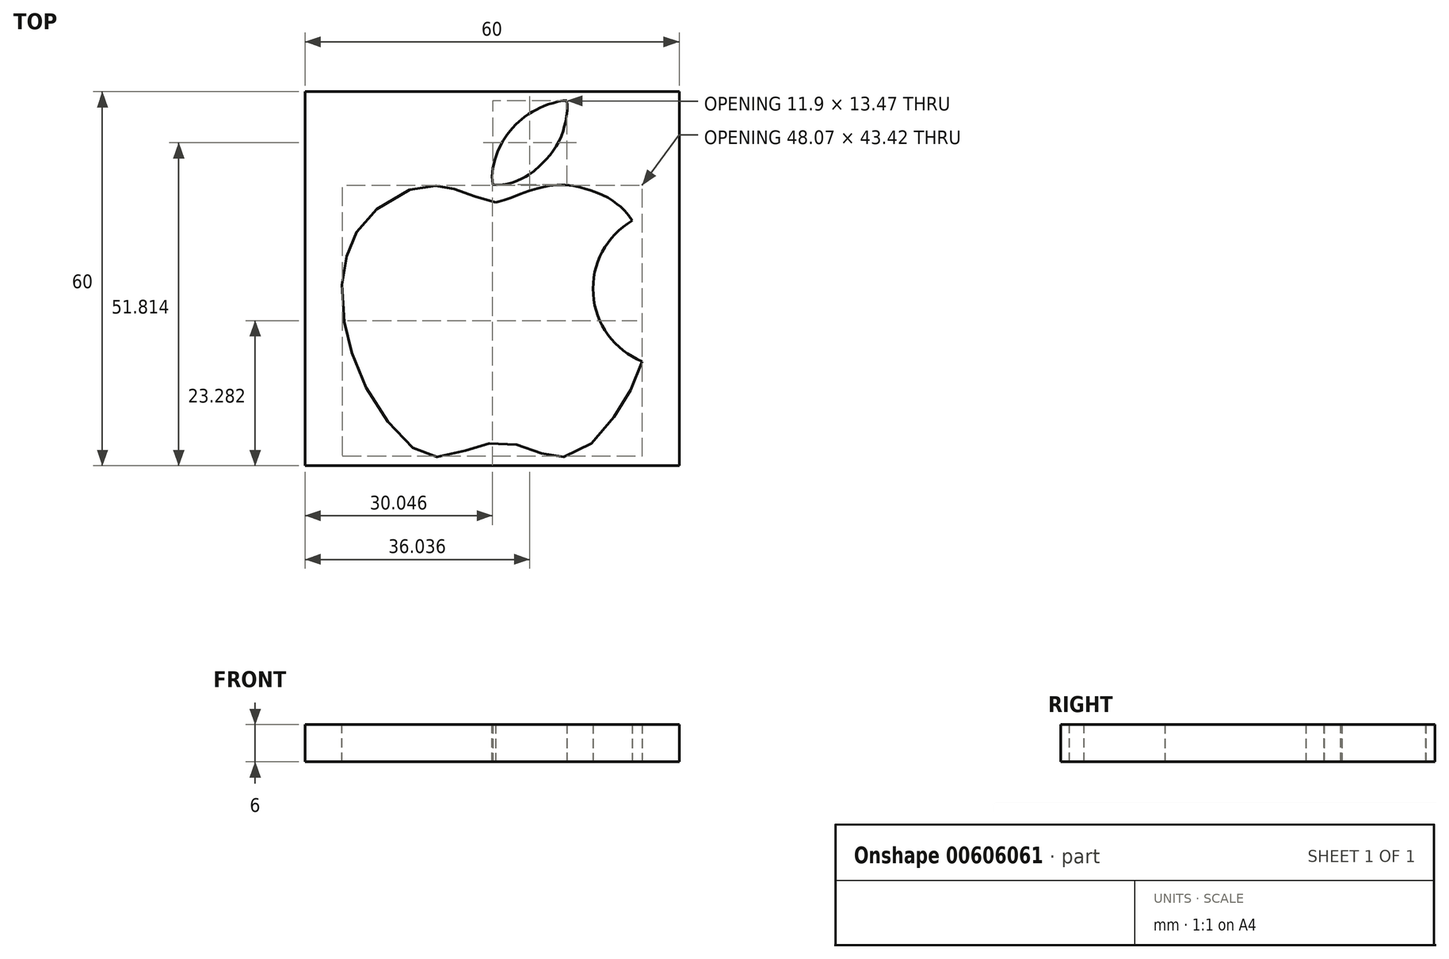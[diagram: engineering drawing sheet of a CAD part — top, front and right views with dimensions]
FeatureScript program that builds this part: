
annotation { "Feature Type Name" : "Feature", "Feature Type Description" : "" }
export const myFeature = defineFeature(function(context is Context, id is Id, definition is map)
    precondition{}
    {
        {
            var Q0;
            Q0=qCreatedBy(makeId("Top.planeOp"),FACE);
            var sketch = newSketch(context, id + "F0", { "sketchPlane" : qUnion([Q0])});
            skArc(sketch, "E0", {"start": v(52.5, 39.31) * mm, "mid": v(46.21, 27.53) * mm, "end": v(54.08, 16.73) * mm});
            skFitSpline(sketch, "E1", {"points": [v(52.5, 39.31) * mm, v(51.55, 40.58) * mm, v(50.61, 41.51) * mm, v(49.89, 42.08) * mm, v(49.02, 42.74) * mm, v(47.59, 43.48) * mm, v(45.89, 44.16) * mm, v(45.13, 44.36) * mm, v(43.9, 44.71) * mm, v(41.52, 45.05) * mm, v(39.07, 44.9) * mm, v(37.73, 44.63) * mm, v(34.98, 43.77) * mm, v(32.17, 42.67) * mm, v(30.95, 42.32) * mm, v(30.54, 42.22) * mm], "startDerivative": vector(-15.07, 19.7) * mm, "endDerivative": vector(-10.88, -2.45) * mm});
            skFitSpline(sketch, "E2", {"points": [v(30.54, 42.22) * mm, v(29.98, 42.25) * mm, v(28.38, 42.84) * mm, v(27.14, 43.26) * mm, v(26.49, 43.5) * mm, v(24.74, 44.13) * mm, v(23.26, 44.54) * mm, v(22.5, 44.63) * mm, v(21.97, 44.79) * mm, v(20.45, 44.9) * mm, v(18.9, 44.63) * mm, v(16.42, 44.16) * mm, v(12.72, 42.25) * mm, v(10.18, 39.76) * mm, v(8.57, 37.95) * mm, v(7.63, 36.17) * mm, v(6.95, 34.5) * mm, v(6.4, 32.55) * mm, v(6.08, 30.67) * mm, v(5.91, 26.78) * mm, v(6.28, 23.1) * mm, v(6.9, 20.17) * mm, v(7.67, 17.64) * mm, v(9.16, 13.85) * mm, v(11.03, 10.37) * mm, v(13.95, 6.25) * mm, v(16.4, 3.55) * mm, v(18.6, 2.05) * mm, v(20.17, 1.5) * mm, v(22.01, 1.45) * mm, v(24.46, 1.98) * mm, v(26.58, 2.78) * mm, v(28.13, 3.32) * mm, v(29.78, 3.63) * mm, v(31.48, 3.76) * mm, v(34.02, 3.36) * mm, v(36.23, 2.58) * mm, v(37.73, 2.06) * mm, v(38.79, 1.74) * mm, v(40.1, 1.5) * mm, v(42, 1.51) * mm, v(44.3, 2.4) * mm, v(46.98, 4.6) * mm, v(49.23, 7.33) * mm, v(50.52, 9.22) * mm, v(52.16, 11.97) * mm, v(52.81, 13.42) * mm, v(54.08, 16.73) * mm], "startDerivative": vector(-45.4, -1.17) * mm, "endDerivative": vector(82.14, 213.58) * mm});
            skFitSpline(sketch, "E3", {"points": [v(30.09, 45.08) * mm, v(30.75, 45.03) * mm, v(32.08, 45.15) * mm, v(32.98, 45.36) * mm, v(33.95, 45.68) * mm, v(34.8, 46.1) * mm, v(35.37, 46.38) * mm, v(35.9, 46.7) * mm, v(37.35, 47.82) * mm, v(39.07, 49.63) * mm, v(39.68, 50.4) * mm, v(40.34, 51.39) * mm, v(40.9, 52.4) * mm, v(41.41, 53.67) * mm, v(41.52, 54.31) * mm, v(41.84, 55.41) * mm, v(42, 56.68) * mm, v(42.05, 57.72) * mm, v(41.99, 58.55) * mm], "startDerivative": vector(13.6, -1.6) * mm, "endDerivative": vector(-1.84, 17) * mm});
            skFitSpline(sketch, "E4", {"points": [v(41.99, 58.55) * mm, v(41.52, 58.55) * mm, v(40.72, 58.44) * mm, v(39.93, 58.24) * mm, v(39.12, 58.03) * mm, v(38.27, 57.7) * mm, v(37.73, 57.45) * mm, v(37.26, 57.23) * mm, v(36.75, 56.97) * mm, v(36.2, 56.64) * mm, v(35.5, 56.18) * mm, v(34.98, 55.8) * mm, v(34.66, 55.54) * mm, v(34.3, 55.25) * mm, v(33.9, 54.84) * mm, v(33.4, 54.31) * mm, v(33.03, 53.9) * mm, v(32.76, 53.58) * mm, v(31.95, 52.4) * mm, v(31.2, 51.1) * mm, v(30.73, 50) * mm, v(30.09, 47.42) * mm, v(30.09, 45.08) * mm], "startDerivative": vector(-11.77, 0.57) * mm, "endDerivative": vector(5.2, -28.03) * mm});
            skLineSegment(sketch, "E5.bottom", {"start": v(0, 0) * mm, "end": v(60, 0) * mm});
            skLineSegment(sketch, "E5.top", {"start": v(0, 60) * mm, "end": v(60, 60) * mm});
            skLineSegment(sketch, "E5.left", {"start": v(0, 0) * mm, "end": v(0, 60) * mm});
            skLineSegment(sketch, "E5.right", {"start": v(60, 0) * mm, "end": v(60, 60) * mm});
            skSolve(sketch);
        }
        {
            var Q0;
            Q0 = qSketchRegion(id + "F0", true);
            extrude(context, id + "F1", {"entities" : qUnion([Q0]), "depth" : 6 * mm, "offsetDistance" : 25 * mm});
        }
    });
